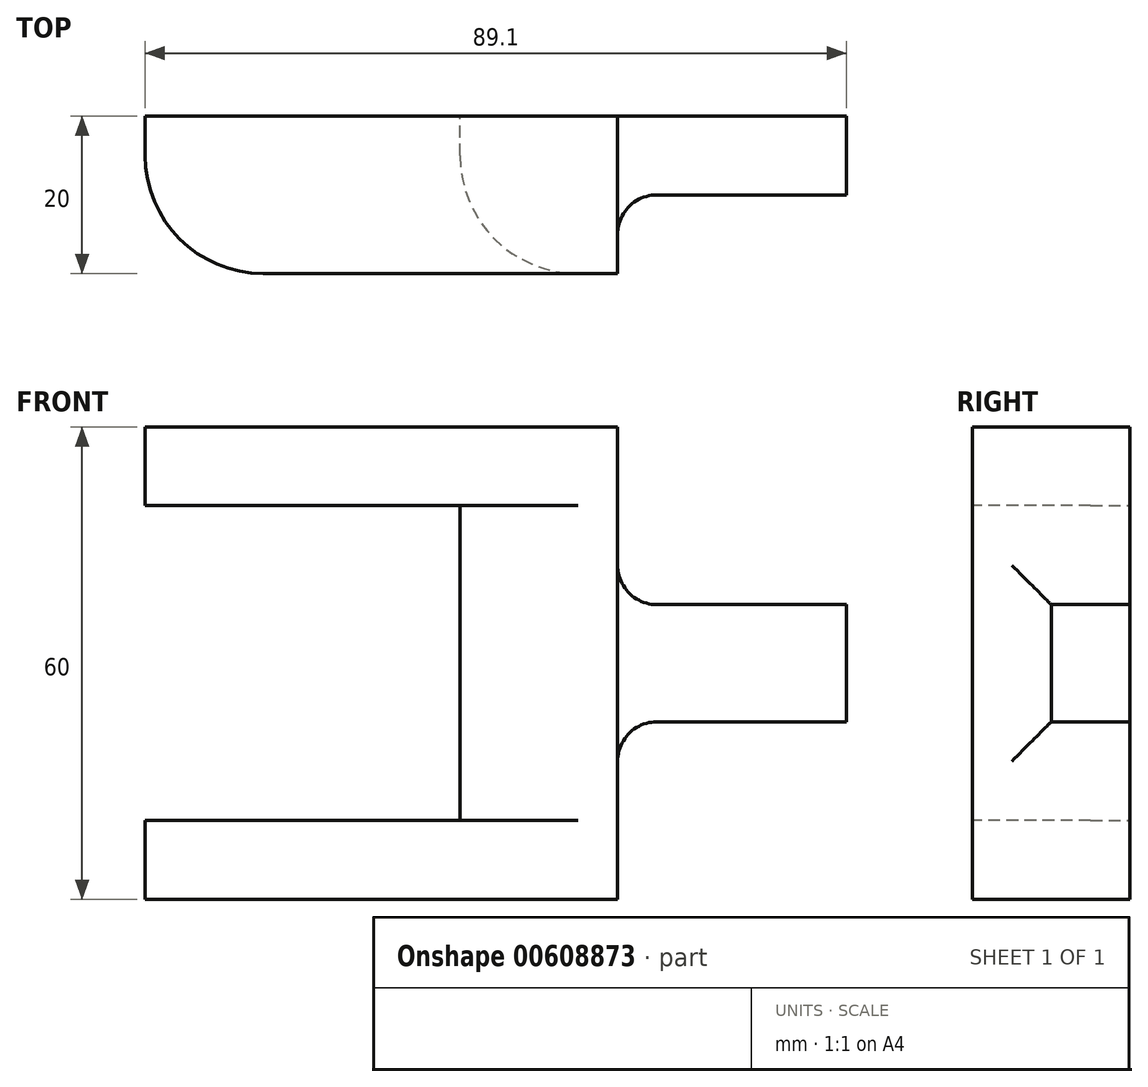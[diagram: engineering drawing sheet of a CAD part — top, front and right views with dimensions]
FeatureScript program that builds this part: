
annotation { "Feature Type Name" : "Feature", "Feature Type Description" : "" }
export const myFeature = defineFeature(function(context is Context, id is Id, definition is map)
    precondition{}
    {
        {
            var Q0;
            Q0=qCreatedBy(makeId("Front.planeOp"),FACE);
            var sketch = newSketch(context, id + "F0", { "sketchPlane" : qUnion([Q0])});
            skLineSegment(sketch, "E0.bottom", {"start": v(-30, 30) * mm, "end": v(30, 30) * mm});
            skLineSegment(sketch, "E0.top", {"start": v(-30, -30) * mm, "end": v(30, -30) * mm});
            skLineSegment(sketch, "E0.left", {"start": v(-30, 30) * mm, "end": v(-30, -30) * mm});
            skLineSegment(sketch, "E0.right", {"start": v(30, 30) * mm, "end": v(30, -30) * mm});
            skPoint(sketch, "E0.middle", {"position": v(0, 0) * mm});
            skLineSegment(sketch, "E1.bottom", {"start": v(-30, 20.05) * mm, "end": v(10, 20.05) * mm});
            skLineSegment(sketch, "E1.top", {"start": v(-30, -19.95) * mm, "end": v(10, -19.95) * mm});
            skLineSegment(sketch, "E1.left", {"start": v(-30, 20.05) * mm, "end": v(-30, -19.95) * mm});
            skLineSegment(sketch, "E1.right", {"start": v(10, 20.05) * mm, "end": v(10, -19.95) * mm});
            skSolve(sketch);
        }
        {
            var Q0;
            {var subQ4=sQuery(id+"F0.wireOp",EDGE,"E0.bottom");Q0=makeQuery(id+"F0.imprint","IMPRINT",FACE,{"disambiguationData":[TD([[makeQuery(id+"F0.imprint","IMPRINT",EDGE,{"derivedFrom":subQ4}),-1.0]])]});}
            extrude(context, id + "F1", {"entities" : qUnion([Q0]), "depth" : 20 * mm, "offsetDistance" : 25 * mm});
        }
        {
            var Q0;
            Q0=makeQuery(id+"F1.opExtrude","CAP_EDGE",EDGE,{"disambiguationData":[OSD([sQuery(id+"F0.wireOp",EDGE,"E1.right")])],"isStart":false});
            var Q1;
            {var subQ0=sQuery(id+"F0.wireOp",EDGE,"E0.left");Q1=makeQuery(id+"F1.opExtrude","CAP_EDGE",EDGE,{"disambiguationData":[OSD([subQ0]),TDD([makeQuery(id+"F0.imprint","IMPRINT",EDGE,{"disambiguationData":[TD([[makeQuery(id+"F0.imprint","INTERSECT",VERTEX,{"derivedFrom":[sQuery(id+"F0.wireOp",EDGE,"E0.top"),subQ0]}),1.0]])],"derivedFrom":subQ0})])],"isStart":false});}
            var Q2;
            {var subQ0=sQuery(id+"F0.wireOp",EDGE,"E0.left");Q2=makeQuery(id+"F1.opExtrude","CAP_EDGE",EDGE,{"disambiguationData":[OSD([subQ0]),TDD([makeQuery(id+"F0.imprint","IMPRINT",EDGE,{"disambiguationData":[TD([[makeQuery(id+"F0.imprint","INTERSECT",VERTEX,{"derivedFrom":[sQuery(id+"F0.wireOp",EDGE,"E0.bottom"),subQ0]}),-1.0]])],"derivedFrom":subQ0})])],"isStart":false});}
            fillet(context, id + "F2", {"entities" : qUnion([Q0, Q1, Q2]), "radius" : 15 * mm, "tangentPropagation" : true, "allowEdgeOverflow" : false});
        }
        {
            var Q0;
            Q0=qCreatedBy(makeId("Front.planeOp"),FACE);
            var sketch = newSketch(context, id + "F3", { "sketchPlane" : qUnion([Q0])});
            skLineSegment(sketch, "E2.bottom", {"start": v(59.1, 7.44) * mm, "end": v(28.14, 7.44) * mm});
            skLineSegment(sketch, "E2.top", {"start": v(59.1, -7.44) * mm, "end": v(28.14, -7.44) * mm});
            skLineSegment(sketch, "E2.left", {"start": v(59.1, 7.44) * mm, "end": v(59.1, -7.44) * mm});
            skLineSegment(sketch, "E2.right", {"start": v(28.14, 7.44) * mm, "end": v(28.14, -7.44) * mm});
            skPoint(sketch, "E2.middle", {"position": v(43.62, 0) * mm});
            skSolve(sketch);
        }
        {
            var Q0;
            Q0=makeQuery(id+"F3.imprint","IMPRINT",FACE,{"disambiguationData":[TD([[makeQuery(id+"F3.imprint","IMPRINT",EDGE,{"derivedFrom":sQuery(id+"F3.wireOp",EDGE,"E2.bottom")}),1.0]])]});
            extrude(context, id + "F4", {"entities" : qUnion([Q0]), "operationType" : NewBodyOperationType.ADD, "depth" : 10 * mm, "offsetDistance" : 25 * mm});
        }
        {
            var Q0;
            Q0=makeQuery(id+"F4.boolean.opBoolean","INTERSECT",EDGE,{"derivedFrom":[makeQuery(id+"F1.opExtrude","SWEPT_FACE",FACE,{"disambiguationData":[OSD([sQuery(id+"F0.wireOp",EDGE,"E0.right")])]}),makeQuery(id+"F4.opExtrude","SWEPT_FACE",FACE,{"disambiguationData":[OSD([sQuery(id+"F3.wireOp",EDGE,"E2.bottom")])]})]});
            var Q1;
            Q1=makeQuery(id+"F4.boolean.opBoolean","INTERSECT",EDGE,{"derivedFrom":[makeQuery(id+"F1.opExtrude","SWEPT_FACE",FACE,{"disambiguationData":[OSD([sQuery(id+"F0.wireOp",EDGE,"E0.right")])]}),makeQuery(id+"F4.opExtrude","CAP_FACE",FACE,{"disambiguationData":[OSD([sQuery(id+"F3.wireOp",EDGE,"E2.bottom"),sQuery(id+"F3.wireOp",EDGE,"E2.top"),sQuery(id+"F3.wireOp",EDGE,"E2.left"),sQuery(id+"F3.wireOp",EDGE,"E2.right")])],"isStart":false})]});
            var Q2;
            Q2=makeQuery(id+"F4.boolean.opBoolean","INTERSECT",EDGE,{"derivedFrom":[makeQuery(id+"F1.opExtrude","SWEPT_FACE",FACE,{"disambiguationData":[OSD([sQuery(id+"F0.wireOp",EDGE,"E0.right")])]}),makeQuery(id+"F4.opExtrude","SWEPT_FACE",FACE,{"disambiguationData":[OSD([sQuery(id+"F3.wireOp",EDGE,"E2.top")])]})]});
            fillet(context, id + "F5", {"entities" : qUnion([Q0, Q1, Q2]), "radius" : 5 * mm, "tangentPropagation" : true, "allowEdgeOverflow" : false});
        }
    });
